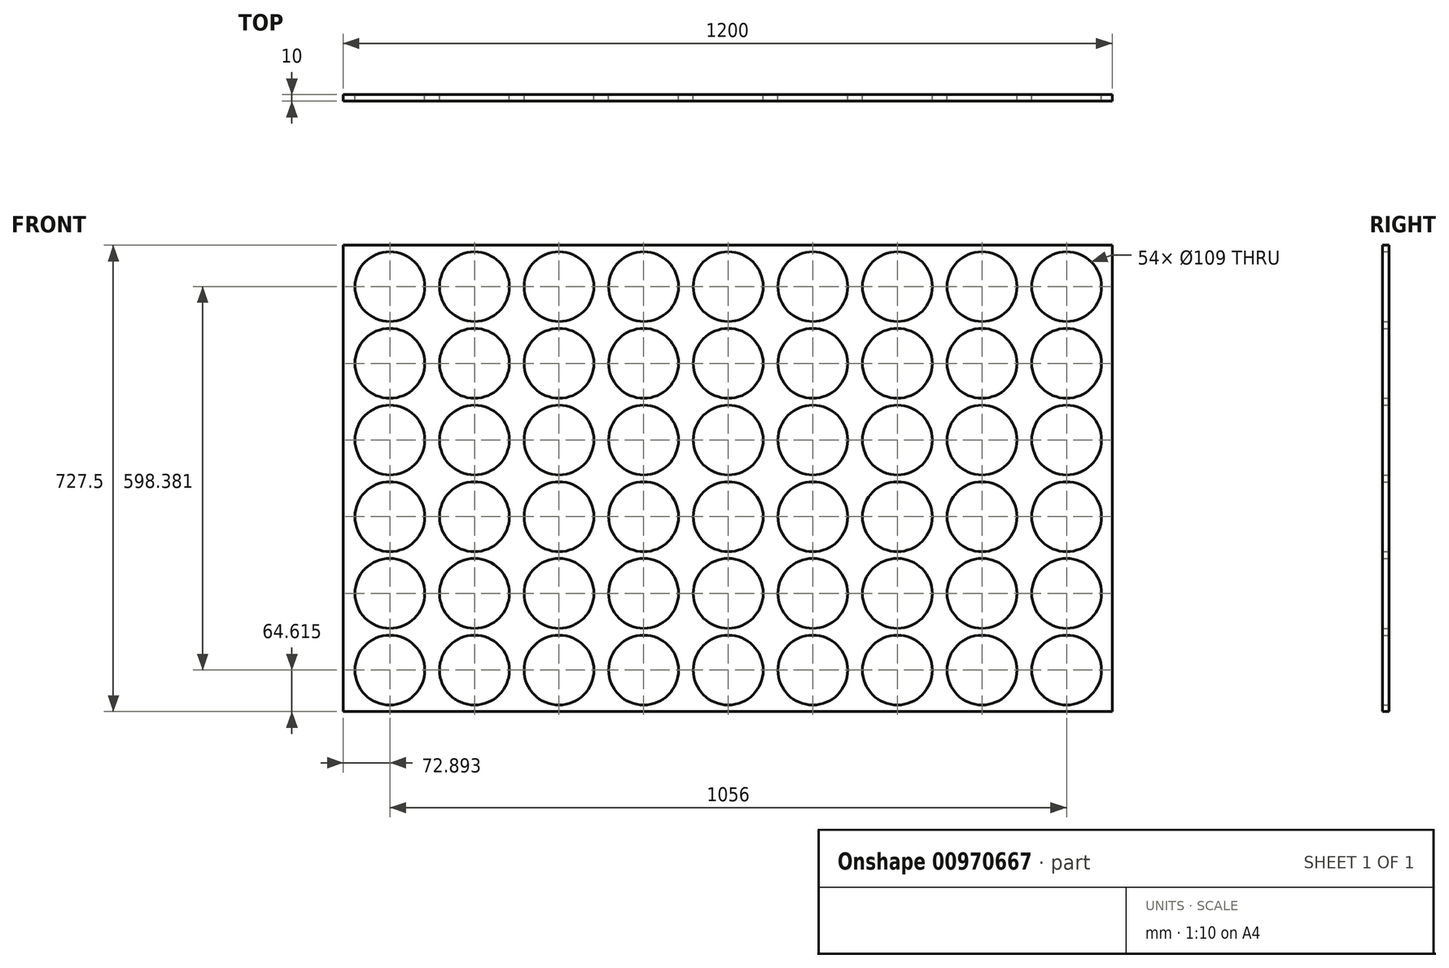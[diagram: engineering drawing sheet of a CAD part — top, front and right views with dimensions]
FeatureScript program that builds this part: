
annotation { "Feature Type Name" : "Feature", "Feature Type Description" : "" }
export const myFeature = defineFeature(function(context is Context, id is Id, definition is map)
    precondition{}
    {
        {
            var Q0;
            Q0=qCreatedBy(makeId("Front.planeOp"),FACE);
            var sketch = newSketch(context, id + "F0", { "sketchPlane" : qUnion([Q0])});
            skLineSegment(sketch, "E0.bottom", {"start": v(-595.74, 332.63) * mm, "end": v(604.26, 332.63) * mm});
            skLineSegment(sketch, "E0.top", {"start": v(-595.74, -394.87) * mm, "end": v(604.26, -394.87) * mm});
            skLineSegment(sketch, "E0.left", {"start": v(-595.74, 332.63) * mm, "end": v(-595.74, -394.87) * mm});
            skLineSegment(sketch, "E0.right", {"start": v(604.26, 332.63) * mm, "end": v(604.26, -394.87) * mm});
            skSolve(sketch);
        }
        {
            var Q0;
            Q0=makeQuery(id+"F0.imprint","IMPRINT",FACE,{"disambiguationData":[TD([[makeQuery(id+"F0.imprint","IMPRINT",EDGE,{"derivedFrom":sQuery(id+"F0.wireOp",EDGE,"E0.bottom")}),-1.0]])]});
            extrude(context, id + "F1", {"entities" : qUnion([Q0]), "depth" : 10 * mm, "offsetDistance" : 25 * mm});
        }
        {
            var Q0;
            Q0=makeQuery(id+"F0.imprint","IMPRINT",FACE,{"disambiguationData":[TD([[makeQuery(id+"F0.imprint","IMPRINT",EDGE,{"derivedFrom":sQuery(id+"F0.wireOp",EDGE,"E0.bottom")}),-1.0]])]});
            var sketch = newSketch(context, id + "F2", { "sketchPlane" : qUnion([Q0])});
            skLineSegment(sketch, "E1.0", {"start": v(-595.74, -384.87) * mm, "end": v(602.48, -384.87) * mm});
            skLineSegment(sketch, "E1.2", {"start": v(-595.74, 322.63) * mm, "end": v(604.26, 322.63) * mm});
            skLineSegment(sketch, "E2.0", {"start": v(604.26, 332.63) * mm, "end": v(604.26, -394.87) * mm});
            skLineSegment(sketch, "E3.0", {"start": v(-595.74, 332.63) * mm, "end": v(-595.74, -394.87) * mm});
            skLineSegment(sketch, "E4.6.0.0", {"start": v(-331.3, 345.13) * mm, "end": v(-331.3, -384.87) * mm});
            skLineSegment(sketch, "E4.7.0.0", {"start": v(-453.51, 356.6) * mm, "end": v(-453.51, -373.4) * mm});
            skLineSegment(sketch, "E4.direction1", {"start": v(471.26, -384.87) * mm, "end": v(338.26, -384.87) * mm, "construction": true});
            skLineSegment(sketch, "E5.0", {"start": v(462.04, 345.13) * mm, "end": v(462.04, -384.87) * mm});
            skLineSegment(sketch, "E6.0", {"start": v(472.04, 345.13) * mm, "end": v(472.04, -384.87) * mm});
            skLineSegment(sketch, "E7.0", {"start": v(329.82, 345.13) * mm, "end": v(329.82, -384.87) * mm});
            skLineSegment(sketch, "E8.0", {"start": v(339.82, 345.13) * mm, "end": v(339.82, -384.87) * mm});
            skLineSegment(sketch, "E9.0", {"start": v(197.6, 345.13) * mm, "end": v(197.6, -384.87) * mm});
            skLineSegment(sketch, "E10.0", {"start": v(207.6, 345.13) * mm, "end": v(207.6, -384.87) * mm});
            skLineSegment(sketch, "E11.0", {"start": v(67.26, 345.13) * mm, "end": v(67.26, -384.87) * mm});
            skLineSegment(sketch, "E12.0", {"start": v(65.38, 345.13) * mm, "end": v(65.38, -384.87) * mm});
            skLineSegment(sketch, "E13.0", {"start": v(75.38, 345.13) * mm, "end": v(75.38, -384.87) * mm});
            skLineSegment(sketch, "E14.0", {"start": v(-66.85, 345.13) * mm, "end": v(-66.85, -384.87) * mm});
            skLineSegment(sketch, "E15.0", {"start": v(-56.85, 345.13) * mm, "end": v(-56.85, -384.87) * mm});
            skLineSegment(sketch, "E16.0", {"start": v(-199.07, 345.13) * mm, "end": v(-199.07, -384.87) * mm});
            skLineSegment(sketch, "E17.0", {"start": v(-189.07, 345.13) * mm, "end": v(-189.07, -384.87) * mm});
            skLineSegment(sketch, "E18", {"start": v(-321.3, 322.63) * mm, "end": v(-321.3, -384.87) * mm});
            skLineSegment(sketch, "E19", {"start": v(-463.51, -384.87) * mm, "end": v(-463.51, 322.63) * mm});
            skLineSegment(sketch, "E20", {"start": v(594.26, 332.63) * mm, "end": v(594.26, -394.87) * mm});
            skLineSegment(sketch, "E21", {"start": v(-585.74, 356.66) * mm, "end": v(-585.74, -396.16) * mm});
            skLineSegment(sketch, "E22", {"start": v(-585.74, -163.24) * mm, "end": v(-463.51, -163.24) * mm, "construction": true});
            skLineSegment(sketch, "E23", {"start": v(-453.51, -188.01) * mm, "end": v(-331.3, -188.01) * mm, "construction": true});
            skLineSegment(sketch, "E24", {"start": v(-321.3, -174.28) * mm, "end": v(-199.07, -174.28) * mm, "construction": true});
            skLineSegment(sketch, "E25", {"start": v(-199.07, -174.28) * mm, "end": v(-189.07, -174.28) * mm, "construction": true});
            skLineSegment(sketch, "E26", {"start": v(-189.07, -174.28) * mm, "end": v(-66.85, -174.28) * mm, "construction": true});
            skLineSegment(sketch, "E27", {"start": v(-66.85, -174.28) * mm, "end": v(-56.85, -174.28) * mm, "construction": true});
            skLineSegment(sketch, "E28", {"start": v(-56.85, -174.28) * mm, "end": v(65.38, -174.28) * mm, "construction": true});
            skLineSegment(sketch, "E29", {"start": v(65.38, -174.28) * mm, "end": v(75.38, -174.28) * mm, "construction": true});
            skLineSegment(sketch, "E30", {"start": v(75.38, -174.28) * mm, "end": v(197.6, -174.28) * mm, "construction": true});
            skLineSegment(sketch, "E31", {"start": v(197.6, -174.28) * mm, "end": v(207.6, -174.28) * mm, "construction": true});
            skLineSegment(sketch, "E32", {"start": v(207.6, -174.28) * mm, "end": v(329.82, -174.28) * mm, "construction": true});
            skLineSegment(sketch, "E33", {"start": v(329.82, -174.28) * mm, "end": v(339.82, -174.28) * mm, "construction": true});
            skLineSegment(sketch, "E34", {"start": v(339.82, -174.28) * mm, "end": v(462.04, -174.28) * mm, "construction": true});
            skLineSegment(sketch, "E35", {"start": v(594.26, -174.28) * mm, "end": v(604.26, -174.28) * mm, "construction": true});
            skLineSegment(sketch, "E36", {"start": v(594.26, -174.28) * mm, "end": v(472.04, -174.28) * mm, "construction": true});
            skLineSegment(sketch, "E37", {"start": v(533.15, 322.63) * mm, "end": v(533.15, -384.87) * mm, "construction": true});
            skCircle(sketch, "E38", {"center": v(533.15, 268.13) * mm, "radius": 59.5 * mm});
            skCircle(sketch, "E39.0.1.0", {"center": v(533.15, 148.45) * mm, "radius": 59.5 * mm});
            skCircle(sketch, "E39.0.2.0", {"center": v(533.15, 28.77) * mm, "radius": 59.5 * mm});
            skCircle(sketch, "E39.0.3.0", {"center": v(533.15, -90.9) * mm, "radius": 59.5 * mm});
            skCircle(sketch, "E39.0.4.0", {"center": v(533.15, -210.58) * mm, "radius": 59.5 * mm});
            skCircle(sketch, "E39.0.5.0", {"center": v(533.15, -330.26) * mm, "radius": 59.5 * mm});
            skLineSegment(sketch, "E39.direction1", {"start": v(533.15, 268.13) * mm, "end": v(558.15, 268.13) * mm, "construction": true});
            skLineSegment(sketch, "E39.direction2", {"start": v(533.15, 268.13) * mm, "end": v(533.15, 148.45) * mm, "construction": true});
            skLineSegment(sketch, "E40", {"start": v(594.26, 332.63) * mm, "end": v(514.02, 332.63) * mm});
            skSolve(sketch);
        }
        {
            var Q0;
            Q0=makeQuery(id+"F1.opExtrude","CAP_FACE",FACE,{"disambiguationData":[OSD([sQuery(id+"F0.wireOp",EDGE,"E0.bottom"),sQuery(id+"F0.wireOp",EDGE,"E0.top"),sQuery(id+"F0.wireOp",EDGE,"E0.left"),sQuery(id+"F0.wireOp",EDGE,"E0.right")])],"isStart":true});
            var sketch = newSketch(context, id + "F3", { "sketchPlane" : qUnion([Q0])});
            skLineSegment(sketch, "E41.3", {"start": v(590.74, -389.87) * mm, "end": v(-599.26, -389.87) * mm});
            skCircle(sketch, "E42.0", {"center": v(-533.15, 268.13) * mm, "radius": 59.5 * mm, "construction": true});
            skCircle(sketch, "E42.1", {"center": v(-533.15, 148.45) * mm, "radius": 59.5 * mm, "construction": true});
            skCircle(sketch, "E42.2", {"center": v(-533.15, 28.77) * mm, "radius": 59.5 * mm, "construction": true});
            skCircle(sketch, "E42.3", {"center": v(-533.15, -90.9) * mm, "radius": 59.5 * mm, "construction": true});
            skCircle(sketch, "E42.4", {"center": v(-533.15, -210.58) * mm, "radius": 59.5 * mm, "construction": true});
            skCircle(sketch, "E42.5", {"center": v(-533.15, -330.26) * mm, "radius": 59.5 * mm, "construction": true});
            skCircle(sketch, "E43.0", {"center": v(-533.15, 268.13) * mm, "radius": 54.5 * mm});
            skCircle(sketch, "E44.0", {"center": v(-533.15, 148.45) * mm, "radius": 54.5 * mm});
            skCircle(sketch, "E45.0", {"center": v(-533.15, 28.77) * mm, "radius": 54.5 * mm});
            skCircle(sketch, "E46.0", {"center": v(-533.15, -90.9) * mm, "radius": 54.5 * mm});
            skCircle(sketch, "E47.0", {"center": v(-533.15, -210.58) * mm, "radius": 54.5 * mm});
            skCircle(sketch, "E48.0", {"center": v(-533.15, -330.26) * mm, "radius": 54.5 * mm});
            skCircle(sketch, "E49.0", {"center": v(-533.15, -330.26) * mm, "radius": 54.5 * mm, "construction": true});
            skCircle(sketch, "E50.1.0.0", {"center": v(-401.15, -330.26) * mm, "radius": 54.5 * mm});
            skCircle(sketch, "E50.1.0.1", {"center": v(-401.15, -210.58) * mm, "radius": 54.5 * mm});
            skCircle(sketch, "E50.1.0.2", {"center": v(-401.15, -90.9) * mm, "radius": 54.5 * mm});
            skCircle(sketch, "E50.1.0.3", {"center": v(-401.15, 268.13) * mm, "radius": 54.5 * mm});
            skCircle(sketch, "E50.1.0.4", {"center": v(-401.15, 148.45) * mm, "radius": 54.5 * mm});
            skCircle(sketch, "E50.1.0.5", {"center": v(-401.15, 28.77) * mm, "radius": 54.5 * mm});
            skCircle(sketch, "E50.2.0.0", {"center": v(-269.15, -330.26) * mm, "radius": 54.5 * mm});
            skCircle(sketch, "E50.2.0.1", {"center": v(-269.15, -210.58) * mm, "radius": 54.5 * mm});
            skCircle(sketch, "E50.2.0.2", {"center": v(-269.15, -90.9) * mm, "radius": 54.5 * mm});
            skCircle(sketch, "E50.2.0.3", {"center": v(-269.15, 268.13) * mm, "radius": 54.5 * mm});
            skCircle(sketch, "E50.2.0.4", {"center": v(-269.15, 148.45) * mm, "radius": 54.5 * mm});
            skCircle(sketch, "E50.2.0.5", {"center": v(-269.15, 28.77) * mm, "radius": 54.5 * mm});
            skCircle(sketch, "E50.3.0.0", {"center": v(-137.15, -330.26) * mm, "radius": 54.5 * mm});
            skCircle(sketch, "E50.3.0.1", {"center": v(-137.15, -210.58) * mm, "radius": 54.5 * mm});
            skCircle(sketch, "E50.3.0.2", {"center": v(-137.15, -90.9) * mm, "radius": 54.5 * mm});
            skCircle(sketch, "E50.3.0.3", {"center": v(-137.15, 268.13) * mm, "radius": 54.5 * mm});
            skCircle(sketch, "E50.3.0.4", {"center": v(-137.15, 148.45) * mm, "radius": 54.5 * mm});
            skCircle(sketch, "E50.3.0.5", {"center": v(-137.15, 28.77) * mm, "radius": 54.5 * mm});
            skCircle(sketch, "E50.4.0.0", {"center": v(-5.15, -330.26) * mm, "radius": 54.5 * mm});
            skCircle(sketch, "E50.4.0.1", {"center": v(-5.15, -210.58) * mm, "radius": 54.5 * mm});
            skCircle(sketch, "E50.4.0.2", {"center": v(-5.15, -90.9) * mm, "radius": 54.5 * mm});
            skCircle(sketch, "E50.4.0.3", {"center": v(-5.15, 268.13) * mm, "radius": 54.5 * mm});
            skCircle(sketch, "E50.4.0.4", {"center": v(-5.15, 148.45) * mm, "radius": 54.5 * mm});
            skCircle(sketch, "E50.4.0.5", {"center": v(-5.15, 28.77) * mm, "radius": 54.5 * mm});
            skCircle(sketch, "E50.5.0.0", {"center": v(126.85, -330.26) * mm, "radius": 54.5 * mm});
            skCircle(sketch, "E50.5.0.1", {"center": v(126.85, -210.58) * mm, "radius": 54.5 * mm});
            skCircle(sketch, "E50.5.0.2", {"center": v(126.85, -90.9) * mm, "radius": 54.5 * mm});
            skCircle(sketch, "E50.5.0.3", {"center": v(126.85, 268.13) * mm, "radius": 54.5 * mm});
            skCircle(sketch, "E50.5.0.4", {"center": v(126.85, 148.45) * mm, "radius": 54.5 * mm});
            skCircle(sketch, "E50.5.0.5", {"center": v(126.85, 28.77) * mm, "radius": 54.5 * mm});
            skCircle(sketch, "E50.6.0.0", {"center": v(258.85, -330.26) * mm, "radius": 54.5 * mm});
            skCircle(sketch, "E50.6.0.1", {"center": v(258.85, -210.58) * mm, "radius": 54.5 * mm});
            skCircle(sketch, "E50.6.0.2", {"center": v(258.85, -90.9) * mm, "radius": 54.5 * mm});
            skCircle(sketch, "E50.6.0.3", {"center": v(258.85, 268.13) * mm, "radius": 54.5 * mm});
            skCircle(sketch, "E50.6.0.4", {"center": v(258.85, 148.45) * mm, "radius": 54.5 * mm});
            skCircle(sketch, "E50.6.0.5", {"center": v(258.85, 28.77) * mm, "radius": 54.5 * mm});
            skCircle(sketch, "E50.7.0.0", {"center": v(390.85, -330.26) * mm, "radius": 54.5 * mm});
            skCircle(sketch, "E50.7.0.1", {"center": v(390.85, -210.58) * mm, "radius": 54.5 * mm});
            skCircle(sketch, "E50.7.0.2", {"center": v(390.85, -90.9) * mm, "radius": 54.5 * mm});
            skCircle(sketch, "E50.7.0.3", {"center": v(390.85, 268.13) * mm, "radius": 54.5 * mm});
            skCircle(sketch, "E50.7.0.4", {"center": v(390.85, 148.45) * mm, "radius": 54.5 * mm});
            skCircle(sketch, "E50.7.0.5", {"center": v(390.85, 28.77) * mm, "radius": 54.5 * mm});
            skCircle(sketch, "E50.8.0.0", {"center": v(522.85, -330.26) * mm, "radius": 54.5 * mm});
            skCircle(sketch, "E50.8.0.1", {"center": v(522.85, -210.58) * mm, "radius": 54.5 * mm});
            skCircle(sketch, "E50.8.0.2", {"center": v(522.85, -90.9) * mm, "radius": 54.5 * mm});
            skCircle(sketch, "E50.8.0.3", {"center": v(522.85, 268.13) * mm, "radius": 54.5 * mm});
            skCircle(sketch, "E50.8.0.4", {"center": v(522.85, 148.45) * mm, "radius": 54.5 * mm});
            skCircle(sketch, "E50.8.0.5", {"center": v(522.85, 28.77) * mm, "radius": 54.5 * mm});
            skLineSegment(sketch, "E50.direction1", {"start": v(-533.15, -330.26) * mm, "end": v(-401.15, -330.26) * mm, "construction": true});
            skSolve(sketch);
        }
        {
            var Q0;
            Q0 = qSketchRegion(id + "F3", true);
            extrude(context, id + "F4", {"entities" : qUnion([Q0]), "operationType" : NewBodyOperationType.REMOVE, "endBound" : BoundingType.THROUGH_ALL, "oppositeDirection" : true, "depth" : 25 * mm, "offsetDistance" : 25 * mm});
        }
    });
